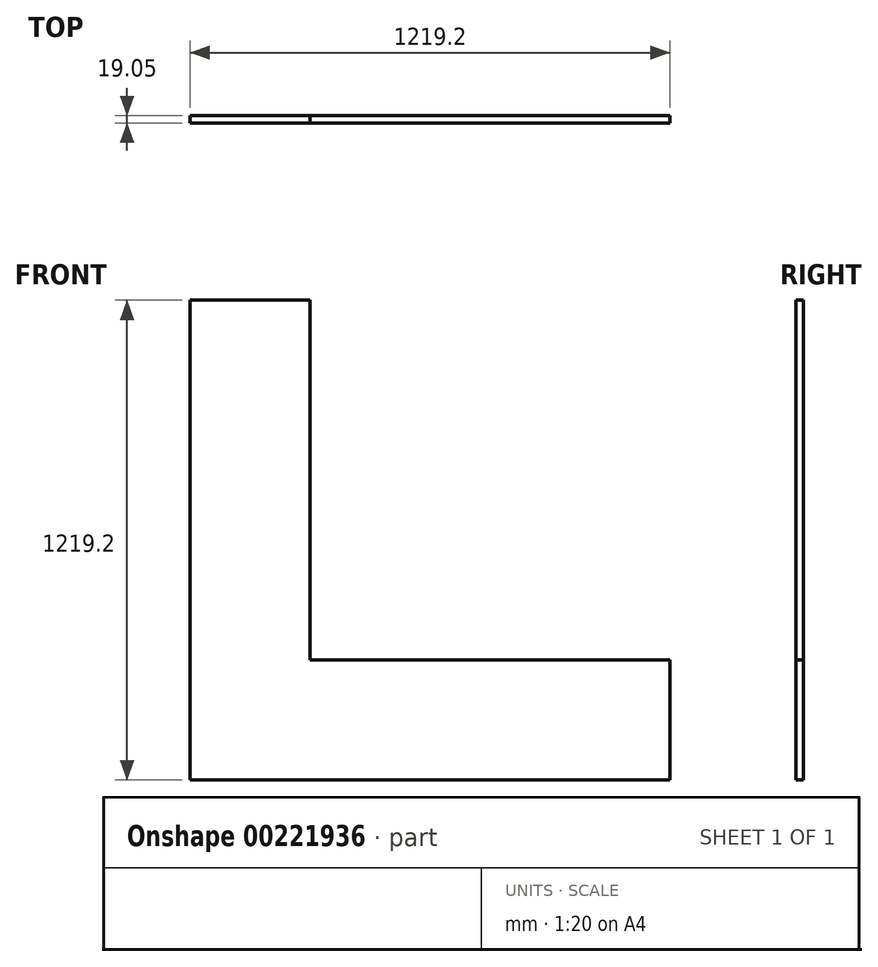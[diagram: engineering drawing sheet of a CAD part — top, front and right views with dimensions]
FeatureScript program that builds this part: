
annotation { "Feature Type Name" : "Feature", "Feature Type Description" : "" }
export const myFeature = defineFeature(function(context is Context, id is Id, definition is map)
    precondition{}
    {
        {
            var Q0;
            Q0=qCreatedBy(makeId("Front.planeOp"),FACE);
            var sketch = newSketch(context, id + "F0", { "sketchPlane" : qUnion([Q0])});
            skLineSegment(sketch, "E0.bottom", {"start": v(-778.6, 561.12) * mm, "end": v(-473.8, 561.12) * mm});
            skLineSegment(sketch, "E0.top", {"start": v(-778.6, -658.08) * mm, "end": v(440.6, -658.08) * mm});
            skLineSegment(sketch, "E0.left", {"start": v(-778.6, 561.12) * mm, "end": v(-778.6, -658.08) * mm});
            skLineSegment(sketch, "E0.right", {"start": v(440.6, -353.28) * mm, "end": v(440.6, -658.08) * mm});
            skLineSegment(sketch, "E1.0", {"start": v(-473.8, 561.12) * mm, "end": v(-473.8, -353.28) * mm});
            skLineSegment(sketch, "E2.0", {"start": v(-473.8, -353.28) * mm, "end": v(440.6, -353.28) * mm});
            skPoint(sketch, "E3.orphan", {"position": v(440.6, 561.12) * mm});
            skSolve(sketch);
        }
        {
            var Q0;
            Q0=makeQuery(id+"F0.imprint","IMPRINT",FACE,{"disambiguationData":[TD([[makeQuery(id+"F0.imprint","IMPRINT",EDGE,{"derivedFrom":sQuery(id+"F0.wireOp",EDGE,"E0.bottom")}),-1.0]])]});
            extrude(context, id + "F1", {"entities" : qUnion([Q0]), "depth" : 19.05 * mm});
        }
    });
